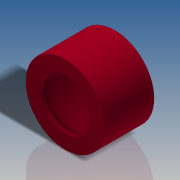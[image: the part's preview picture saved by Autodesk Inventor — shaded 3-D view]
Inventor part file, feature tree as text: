
AUTODESK INVENTOR PART (.ipt)
format: ipt  version: 2016 SP2 (Build 200236200, 236)  size: 151,040 bytes
history: native  units: in
note: dims shown in document units (in); Inventor stores cm internally (conversion verified against a paired STEP export)
features: revolve x1, fillet x1, sketch x1
ambient origin geometry x8: Origin, YZ Plane, XZ Plane, XY Plane, X Axis, Y Axis, Z Axis, Center Point
bodies: Solid1 (feature_tree)
feature tree (3):
  revolve  "Revolution1"  [1 undecoded]
  fillet  "Fillet1"  Radius=0.0315in
  sketch  "Sketch2"  dims[d0=0.5984in d1=0.378in d2=0.0315in d3=0.378in d4=0.5039in d5=90.0deg d6=0.0039in]
note: 1 required parameter value undecoded (feature->parameter linkage not recoverable at this tier; creation-order binding heuristic only, values carry confidence <= 0.55)
